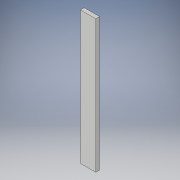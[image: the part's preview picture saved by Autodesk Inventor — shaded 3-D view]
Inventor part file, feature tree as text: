
AUTODESK INVENTOR PART (.ipt)
format: ipt  version: 2019 (Build 230136000, 136)  size: 109,056 bytes
history: native  units: in
note: dims shown in document units (in); Inventor stores cm internally (conversion verified against a paired STEP export)
features: sketch x2, extrude x1, hole x1, projected_geometry x1
ambient origin geometry x8: Origin, YZ Plane, XZ Plane, XY Plane, X Axis, Y Axis, Z Axis, Center Point
bodies: Solid1 (feature_tree)
feature tree (5):
  extrude  "Extrusion1"  Depth=13.0in
  hole  "Hole1"  [1 undecoded]
  sketch  "Sketch1"  dims[d0=1.5in d1=13.0in]
  sketch  "Sketch2"  dims[d2=0.375in d3=0.0in d4=1.0in d5=1.5in d6=0.375in d7=0.25in d8=0.1875in d9=0.1875in d10=0.145in d11=0.38in d12=0.375in d13=0.25in d14=0.5635in d15=1.0in d16=0.8108in]
  projected_geometry  "Projected Loop1"
note: 1 required parameter value undecoded (feature->parameter linkage not recoverable at this tier; creation-order binding heuristic only, values carry confidence <= 0.55)
